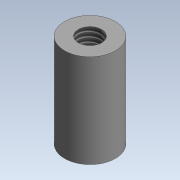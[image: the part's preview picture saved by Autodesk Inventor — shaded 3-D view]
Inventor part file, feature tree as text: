
AUTODESK INVENTOR PART (.ipt)
format: ipt  version: 2020 (Build 240168000, 168)  size: 150,016 bytes
history: native  units: mm
features: extrude x2, sketch x2, thread x1
ambient origin geometry x8: Origin, YZ Plane, XZ Plane, XY Plane, X Axis, Y Axis, Z Axis, Center Point
bodies: Solid1 (feature_tree)
feature tree (5):
  extrude  "Extrusion1"  Depth=8.0mm TaperAngle=0.0deg
  extrude  "Extrusion2"  TaperAngle=0.0deg  [1 undecoded]
  thread  "Thread1"  [1 undecoded]
  sketch  "Sketch1"  dims[d0=4.35mm d1=8.0mm d2=0.0mm]
  sketch  "Sketch2"  dims[d4=2.0mm d5=0.0mm d6=0.0mm d7=8.0mm d8=0.0mm]
note: 2 required parameter values undecoded (feature->parameter linkage not recoverable at this tier; creation-order binding heuristic only, values carry confidence <= 0.55)
